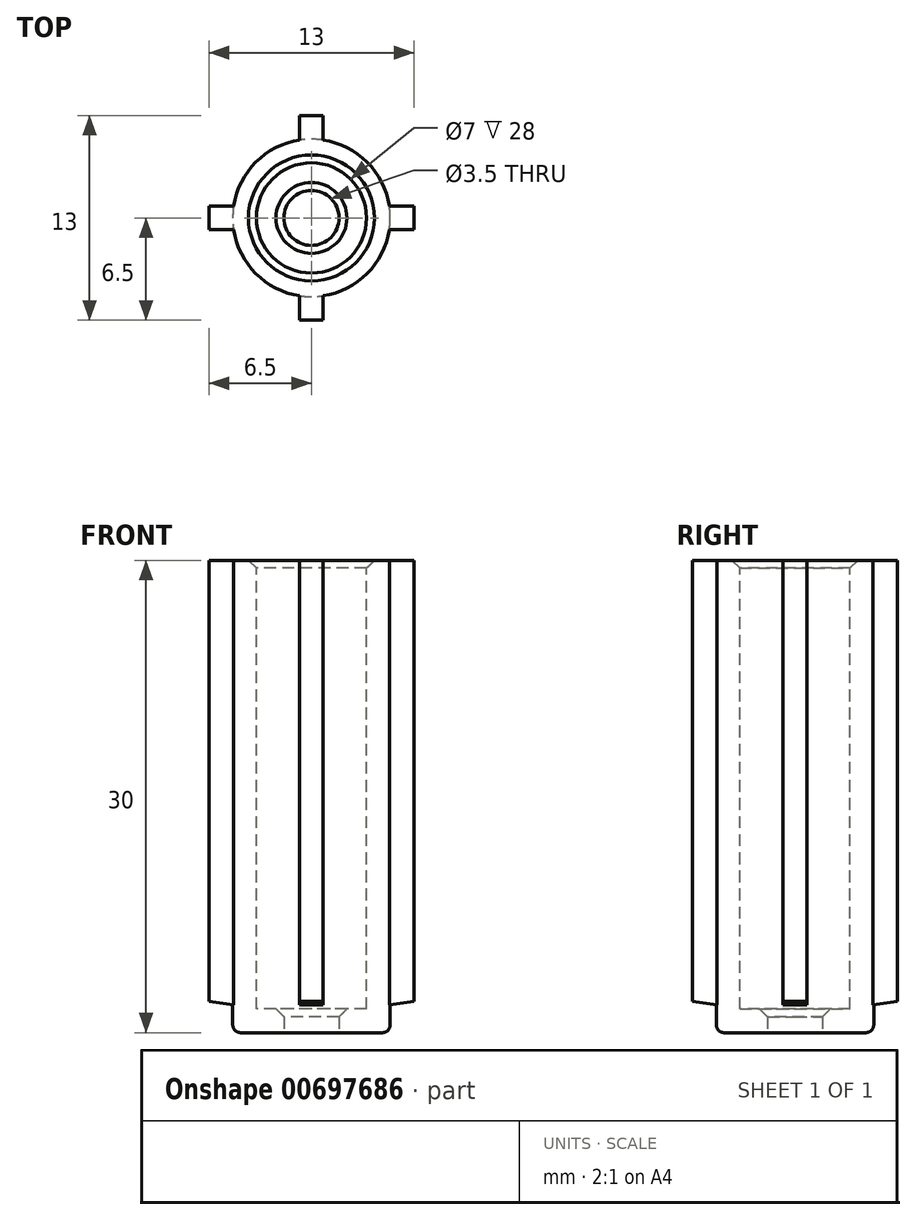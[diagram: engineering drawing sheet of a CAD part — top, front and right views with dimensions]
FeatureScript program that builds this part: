
annotation { "Feature Type Name" : "Feature", "Feature Type Description" : "" }
export const myFeature = defineFeature(function(context is Context, id is Id, definition is map)
    precondition{}
    {
        {
            var Q0;
            Q0=qCreatedBy(makeId("Top.planeOp"),FACE);
            cPlane(context, id + "F0", {"entities" : qUnion([Q0]), "cplaneType" : CPlaneType.OFFSET, "offset" : 0 * mm, "width" : 150 * mm, "height" : 150 * mm});
        }
        {
            var Q0;
            Q0=qCreatedBy(id+"F0.planeOp",FACE);
            var sketch = newSketch(context, id + "F1", { "sketchPlane" : qUnion([Q0])});
            skCircle(sketch, "E0", {"center": v(-25, 25) * mm, "radius": 5 * mm});
            skCircle(sketch, "E1", {"center": v(-25, 25) * mm, "radius": 3.5 * mm});
            skCircle(sketch, "E2", {"center": v(-25, 25) * mm, "radius": 2.5 * mm, "construction": true});
            skSolve(sketch);
        }
        {
            var Q0;
            Q0 = qSketchRegion(id + "F1", true);
            extrude(context, id + "F2", {"entities" : qUnion([Q0]), "oppositeDirection" : true, "depth" : 30 * mm, "offsetDistance" : 25 * mm});
        }
        {
            var Q0;
            Q0=makeQuery(id+"F2.opExtrude","CAP_FACE",FACE,{"disambiguationData":[OSD([sQuery(id+"F1.wireOp",EDGE,"E0"),sQuery(id+"F1.wireOp",EDGE,"E1")])],"isStart":true});
            cPlane(context, id + "F3", {"entities" : qUnion([Q0]), "cplaneType" : CPlaneType.OFFSET, "offset" : 0 * mm, "width" : 150 * mm, "height" : 150 * mm});
        }
        {
            var Q0;
            Q0=qCreatedBy(id+"F3.planeOp",FACE);
            var sketch = newSketch(context, id + "F4", { "sketchPlane" : qUnion([Q0])});
            skCircle(sketch, "E3.0", {"center": v(-25, 25) * mm, "radius": 3.5 * mm, "construction": true});
            skLineSegment(sketch, "E4.bottom", {"start": v(-25.75, 31.5) * mm, "end": v(-24.25, 31.5) * mm});
            skLineSegment(sketch, "E4.top", {"start": v(-25.75, 28.86) * mm, "end": v(-24.25, 28.86) * mm});
            skLineSegment(sketch, "E4.left", {"start": v(-25.75, 31.5) * mm, "end": v(-25.75, 28.86) * mm});
            skLineSegment(sketch, "E4.right", {"start": v(-24.25, 31.5) * mm, "end": v(-24.25, 28.86) * mm});
            skPoint(sketch, "E5.center", {"position": v(0, 0) * mm});
            skSolve(sketch);
        }
        {
            var Q0;
            Q0 = qSketchRegion(id + "F4", true);
            extrude(context, id + "F5", {"entities" : qUnion([Q0]), "operationType" : NewBodyOperationType.ADD, "oppositeDirection" : true, "depth" : (30 - 0.5) * mm, "offsetDistance" : 25 * mm});
        }
        {
            var Q0;
            Q0=makeQuery(id+"F2.opExtrude","SWEPT_BODY",BODY,{"disambiguationData":[OSD([sQuery(id+"F1.wireOp",EDGE,"E0"),sQuery(id+"F1.wireOp",EDGE,"E1")])]});
            var Q1;
            Q1=makeQuery(id+"F2.opExtrude","SWEPT_FACE",FACE,{"disambiguationData":[OSD([sQuery(id+"F1.wireOp",EDGE,"E1")])]});
            circularPattern(context, id + "F6", {"operationType" : NewBodyOperationType.ADD, "entities" : qUnion([Q0]), "axis" : qUnion([Q1]), "angle" : 360 * degree, "instanceCount" : 4, "equalSpace" : true});
        }
        {
            var Q0;
            {var subQ0=makeQuery(id+"F5.boolean.opBoolean","MERGE",FACE,{"derivedFrom":[makeQuery(id+"F2.opExtrude","CAP_FACE",FACE,{"disambiguationData":[OSD([sQuery(id+"F1.wireOp",EDGE,"E0"),sQuery(id+"F1.wireOp",EDGE,"E1")])],"isStart":true}),makeQuery(id+"F5.opExtrude","CAP_FACE",FACE,{"disambiguationData":[OSD([sQuery(id+"F4.wireOp",EDGE,"E4.bottom"),sQuery(id+"F4.wireOp",EDGE,"E4.top"),sQuery(id+"F4.wireOp",EDGE,"E4.left"),sQuery(id+"F4.wireOp",EDGE,"E4.right")])],"isStart":true})]});Q0=makeQuery(id+"F6.boolean.opBoolean","MERGE",FACE,{"derivedFrom":[subQ0,makeQuery(id+"F6.opPattern","COPY",FACE,{"derivedFrom":subQ0,"instanceName":"1"}),makeQuery(id+"F6.opPattern","COPY",FACE,{"derivedFrom":subQ0,"instanceName":"2"}),makeQuery(id+"F6.opPattern","COPY",FACE,{"derivedFrom":subQ0,"instanceName":"3"})]});}
            cPlane(context, id + "F7", {"entities" : qUnion([Q0]), "cplaneType" : CPlaneType.OFFSET, "offset" : 30 * mm, "oppositeDirection" : true, "width" : 150 * mm, "height" : 150 * mm});
        }
        {
            var Q0;
            Q0=qCreatedBy(id+"F7.planeOp",FACE);
            var sketch = newSketch(context, id + "F8", { "sketchPlane" : qUnion([Q0])});
            skCircle(sketch, "E6.0", {"center": v(-25, 25) * mm, "radius": 3.5 * mm});
            skCircle(sketch, "E7", {"center": v(-25, 25) * mm, "radius": 1.75 * mm});
            skSolve(sketch);
        }
        {
            var Q0;
            Q0 = qSketchRegion(id + "F8", true);
            extrude(context, id + "F9", {"entities" : qUnion([Q0]), "operationType" : NewBodyOperationType.ADD, "depth" : 1.5 * mm, "offsetDistance" : 25 * mm});
        }
        {
            var Q0;
            Q0=makeQuery(id+"F6.opPattern","COPY",EDGE,{"derivedFrom":makeQuery(id+"F5.opExtrude","CAP_EDGE",EDGE,{"disambiguationData":[OSD([sQuery(id+"F4.wireOp",EDGE,"E4.bottom")])],"isStart":false}),"instanceName":"1"});
            var Q1;
            Q1=makeQuery(id+"F5.opExtrude","CAP_EDGE",EDGE,{"disambiguationData":[OSD([sQuery(id+"F4.wireOp",EDGE,"E4.bottom")])],"isStart":false});
            var Q2;
            Q2=makeQuery(id+"F6.opPattern","COPY",EDGE,{"derivedFrom":makeQuery(id+"F5.opExtrude","CAP_EDGE",EDGE,{"disambiguationData":[OSD([sQuery(id+"F4.wireOp",EDGE,"E4.bottom")])],"isStart":false}),"instanceName":"3"});
            var Q3;
            Q3=makeQuery(id+"F6.opPattern","COPY",EDGE,{"derivedFrom":makeQuery(id+"F5.opExtrude","CAP_EDGE",EDGE,{"disambiguationData":[OSD([sQuery(id+"F4.wireOp",EDGE,"E4.bottom")])],"isStart":false}),"instanceName":"2"});
            chamfer(context, id + "F10", {"entities" : qUnion([Q0, Q1, Q2, Q3]), "chamferType" : ChamferType.TWO_OFFSETS, "width1" : 1.5 * mm, "oppositeDirection" : false, "width2" : 10 * mm, "tangentPropagation" : true});
        }
        {
            var Q0;
            Q0=makeQuery(id+"F2.opExtrude","CAP_EDGE",EDGE,{"disambiguationData":[OSD([sQuery(id+"F1.wireOp",EDGE,"E1")])],"isStart":true});
            var Q1;
            Q1=makeQuery(id+"F9.opExtrude","CAP_EDGE",EDGE,{"disambiguationData":[OSD([sQuery(id+"F8.wireOp",EDGE,"E7")])],"isStart":false});
            chamfer(context, id + "F11", {"entities" : qUnion([Q0, Q1]), "width" : 0.5 * mm, "tangentPropagation" : true});
        }
        {
            var Q0;
            Q0=makeQuery(id+"F2.opExtrude","CAP_EDGE",EDGE,{"disambiguationData":[OSD([sQuery(id+"F1.wireOp",EDGE,"E0")])],"isStart":false});
            fillet(context, id + "F12", {"entities" : qUnion([Q0]), "radius" : 0.5 * mm, "tangentPropagation" : true, "allowEdgeOverflow" : false});
        }
    });
